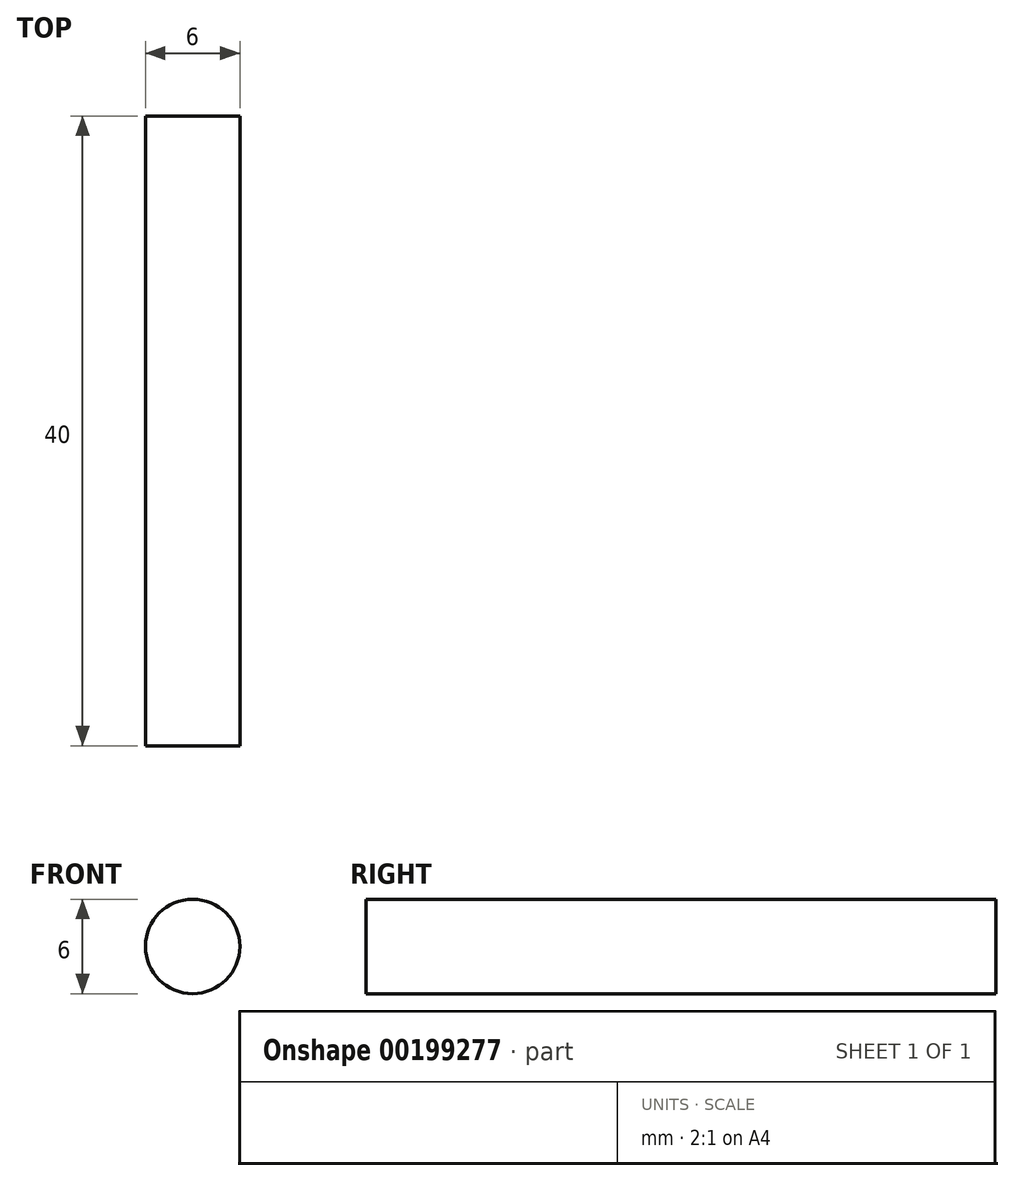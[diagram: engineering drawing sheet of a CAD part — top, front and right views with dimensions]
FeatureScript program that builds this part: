
annotation { "Feature Type Name" : "Feature", "Feature Type Description" : "" }
export const myFeature = defineFeature(function(context is Context, id is Id, definition is map)
    precondition{}
    {
        {
            var Q0;
            Q0=qCreatedBy(makeId("Front.planeOp"),FACE);
            var sketch = newSketch(context, id + "F0", { "sketchPlane" : qUnion([Q0])});
            skCircle(sketch, "E0", {"center": v(0, 0) * mm, "radius": 3 * mm});
            skSolve(sketch);
        }
        {
            var Q0;
            Q0 = qSketchRegion(id + "F0", true);
            extrude(context, id + "F1", {"entities" : qUnion([Q0]), "depth" : 40 * mm});
        }
    });
